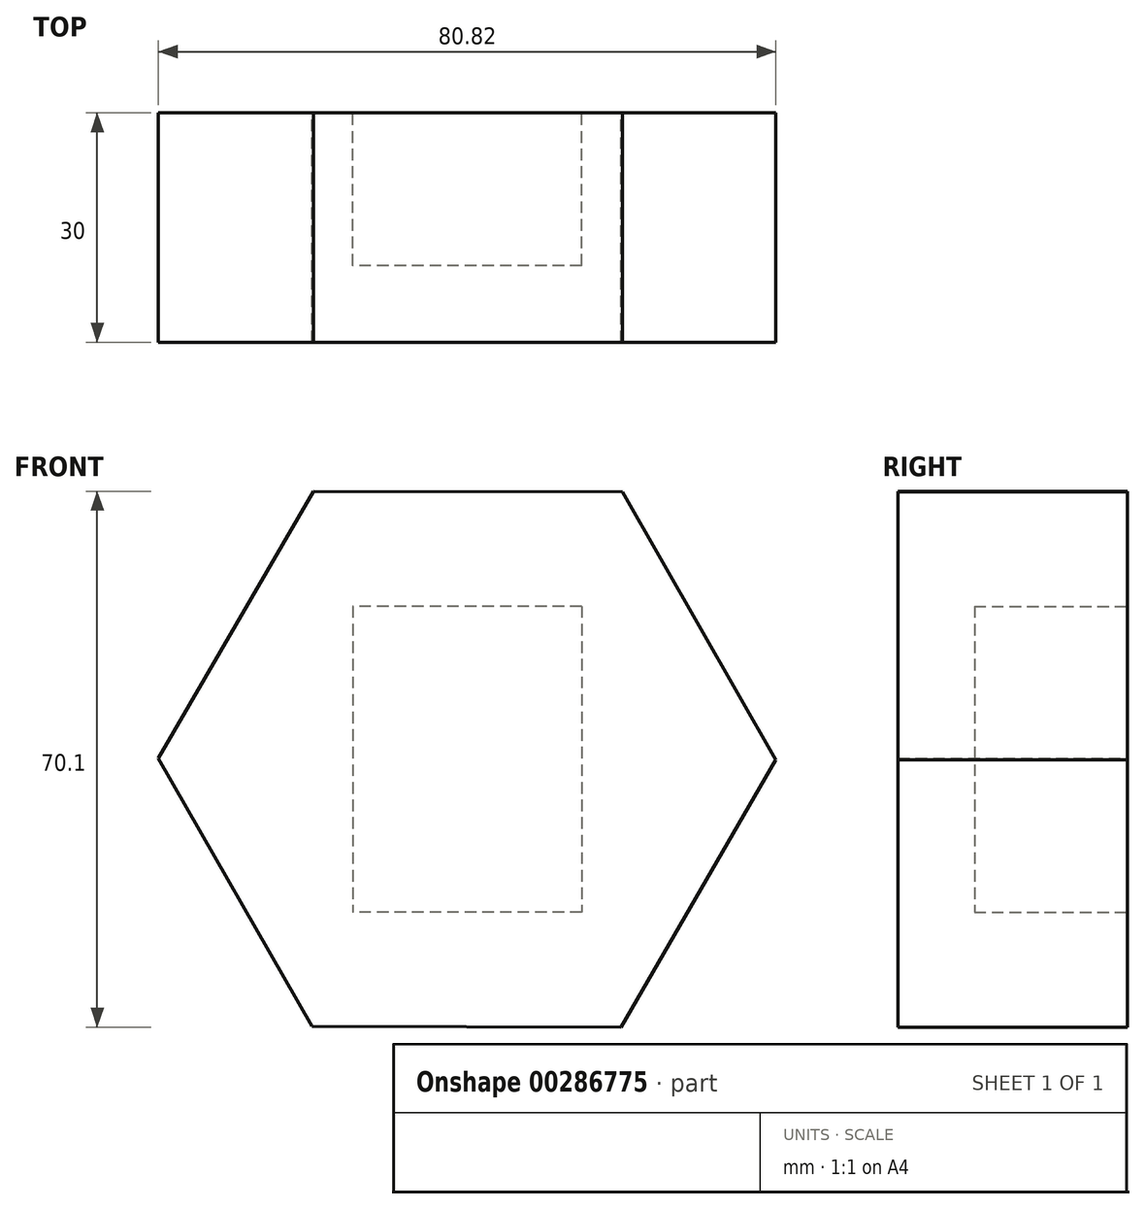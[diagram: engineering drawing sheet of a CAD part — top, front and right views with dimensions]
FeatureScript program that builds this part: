
annotation { "Feature Type Name" : "Feature", "Feature Type Description" : "" }
export const myFeature = defineFeature(function(context is Context, id is Id, definition is map)
    precondition{}
    {
        {
            var Q0;
            Q0=qCreatedBy(makeId("Front.planeOp"),FACE);
            var sketch = newSketch(context, id + "F0", { "sketchPlane" : qUnion([Q0])});
            skCircle(sketch, "E0.cCircle", {"center": v(0, 0) * mm, "radius": 35 * mm, "construction": true});
            skLineSegment(sketch, "E0.0", {"start": v(20.3, 34.95) * mm, "end": v(40.41, -0.1) * mm});
            skLineSegment(sketch, "E0.1", {"start": v(40.41, -0.1) * mm, "end": v(20.11, -35.05) * mm});
            skLineSegment(sketch, "E0.2", {"start": v(20.11, -35.05) * mm, "end": v(-20.3, -34.95) * mm});
            skLineSegment(sketch, "E0.3", {"start": v(-20.3, -34.95) * mm, "end": v(-40.41, 0.1) * mm});
            skLineSegment(sketch, "E0.4", {"start": v(-40.41, 0.1) * mm, "end": v(-20.11, 35.05) * mm});
            skLineSegment(sketch, "E0.5", {"start": v(-20.11, 35.05) * mm, "end": v(20.3, 34.95) * mm});
            skPoint(sketch, "E0.0.midPoint", {"position": v(30.36, 17.42) * mm});
            skSolve(sketch);
        }
        {
            var Q0;
            Q0=makeQuery(id+"F0.imprint","IMPRINT",FACE,{"disambiguationData":[TD([[makeQuery(id+"F0.imprint","IMPRINT",EDGE,{"derivedFrom":sQuery(id+"F0.wireOp",EDGE,"E0.0")}),-1.0]])]});
            extrude(context, id + "F1", {"entities" : qUnion([Q0]), "depth" : 30 * mm});
        }
        {
            var Q0;
            Q0=qCreatedBy(makeId("Front.planeOp"),FACE);
            var sketch = newSketch(context, id + "F2", { "sketchPlane" : qUnion([Q0])});
            skLineSegment(sketch, "E1.bottom", {"start": v(30.8, 25.64) * mm, "end": v(-30.8, 25.64) * mm});
            skLineSegment(sketch, "E1.top", {"start": v(30.8, -25.64) * mm, "end": v(-30.8, -25.64) * mm});
            skLineSegment(sketch, "E1.left", {"start": v(30.8, 25.64) * mm, "end": v(30.8, -25.64) * mm});
            skLineSegment(sketch, "E1.right", {"start": v(-30.8, 25.64) * mm, "end": v(-30.8, -25.64) * mm});
            skPoint(sketch, "E1.middle", {"position": v(0, 0) * mm});
            skSolve(sketch);
        }
        {
            var Q0;
            Q0=makeQuery(id+"F2.imprint","IMPRINT",FACE,{"disambiguationData":[TD([[makeQuery(id+"F2.imprint","IMPRINT",EDGE,{"derivedFrom":sQuery(id+"F2.wireOp",EDGE,"E1.bottom")}),1.0]])]});
            extrude(context, id + "F3", {"entities" : qUnion([Q0]), "operationType" : NewBodyOperationType.REMOVE, "oppositeDirection" : true, "depth" : 20 * mm});
        }
        {
            var Q0;
            Q0=makeQuery(id+"F1.opExtrude","CAP_FACE",FACE,{"disambiguationData":[OSD([sQuery(id+"F0.wireOp",EDGE,"E0.0"),sQuery(id+"F0.wireOp",EDGE,"E0.1"),sQuery(id+"F0.wireOp",EDGE,"E0.2"),sQuery(id+"F0.wireOp",EDGE,"E0.3"),sQuery(id+"F0.wireOp",EDGE,"E0.4"),sQuery(id+"F0.wireOp",EDGE,"E0.5")])],"isStart":true});
            var sketch = newSketch(context, id + "F4", { "sketchPlane" : qUnion([Q0])});
            skLineSegment(sketch, "E2.bottom", {"start": v(-15, 20) * mm, "end": v(15, 20) * mm});
            skLineSegment(sketch, "E2.top", {"start": v(-15, -20) * mm, "end": v(15, -20) * mm});
            skLineSegment(sketch, "E2.left", {"start": v(-15, 20) * mm, "end": v(-15, -20) * mm});
            skLineSegment(sketch, "E2.right", {"start": v(15, 20) * mm, "end": v(15, -20) * mm});
            skPoint(sketch, "E2.middle", {"position": v(0, 0) * mm});
            skSolve(sketch);
        }
        {
            var Q0;
            Q0=qSketchRegion(id+"F4",true);
            extrude(context, id + "F5", {"entities" : qUnion([Q0]), "operationType" : NewBodyOperationType.REMOVE, "oppositeDirection" : true, "depth" : 20 * mm});
        }
    });
